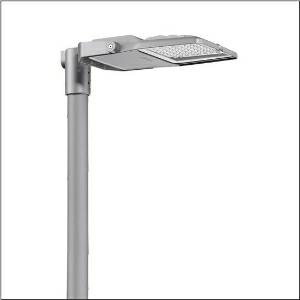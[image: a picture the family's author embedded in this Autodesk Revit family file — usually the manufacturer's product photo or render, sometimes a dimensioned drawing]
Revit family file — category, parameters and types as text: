
# Revit family: floodlight_fl_21_iq_mini___pl33t_5xa7772d4f3a_7ca2
name_source: partatom
category: Lighting Fixtures
units: mm (PartAtom-declared; Revit-internal decimal feet)

## family parameters
Cut with Voids When Loaded = No
Host = Face
Light Source = No
Part Type = Normal
Room Calculation Point = No
Round Connector Dimension = Use Diameter
Shared = No

## types (1)
- --- (1 x LED, 18390 lm, 143 W, 4000K)
    Apparent Load = 143 VA
    CIE Flux Codes = 26 75 99 100 100
    Color Rendering = 70
    Color Temperature = 4000K
    Default Elevation = 1800 mm
    Description = Floodlight FL 21 iQ mini, floodlight, primary light control with lens, of PMMA, primary optical cover: protective disc, of toughened safety glass, transparent, light distribution: PL33T, light emission: direct distribution, installation type: surface-mounted, LED, High Power LED, rated luminous flux: 18.390lm, luminous efficacy: 129lm/W, light colour: 740, colour temperature: 4000K, control gear: iQ Street-Remote/DALI, control: Auto-Match, Temp-Guard, Night-Set, Smart-Wire, Desk-Remote (wireless, voltage-free reading and setting of iQ features in the workshop via application-optimized NFC function/RFID function), optimised constant luminous flux control (CLO 2.0), Light-Fading, Lumen-Switch, with terminal, 6-pole, mains connection: 220..240V, AC, 50/60Hz, start of lifetime: 143W, end of service life: 152W, reduction: 61W, luminaire housing, of diecast aluminium, powder-coated, Siteco® metallic grey (DB 702S), corrosivity category C5 mid according to DIN EN ISO 12944, suitable for swimming pools, chlorine-resistant, sealing non-destructively replaceable, please order mast flange separately, mast bracket, of steel, galvanised, powder-coated, protection rating (complete): IP66, insulation class (complete): insulation class II (safety insulation), certification: CE, ENEC, VDE, protection symbol: D, impact resistance: IK08, permissible operating ambient temperature: -40..+40°C, permissible operating ambient temperature for outdoor applications: -40..+50°C, standard: DIN EN 12944, LABS conformity tested according to VDMA 24364:2018-05, packaging unit: 1 piece

Light Distribution: PL33T
    Height = 70 mm
    Lamp = 1 x LED
    Lamp Light Flux = 18390 lm
    Lamp Power = 143 W
    Lamp count = 1
    Length = 485 mm
    Luminous efficacy = 129 lm/W
    Manufacturer = Siteco
    ModVariant = No
    Model = 5XA7772D4F3A
    Number of Poles = 1
    OnlyDefault = Yes
    Power Factor = 1
    Product Name = Floodlight FL 21 iQ mini | PL33T
    Product group = floodlight | pylon annexe
    ProductGroupID = 6200
    Protection Class = Protection class II
    Protection Degree = IP 66
    RLX_Detail_Level = 1
    RLX_Emergency_Light_Flux = 0 lm
    RLX_Emergency_Type = 0
    RLX_Emergency_Type_DB = No
    RlxData = <blob elided: 101593 chars, md5=c9f020b6>
    Socket = socket
    Standby Power = 0 W
    System Light Flux = 18390 lm
    System Power = 143 W
    Type Comments = factory setting: luminous flux: 100 % | dim-lin: 254 | 730 mA
    Type Image = l_1007125.jpg
    URL = http://relux.com
    VarID = @adj_148780
    Voltage = 0 V
    Weight = 0.00 kg
    Width = 337 mm

## geometry (parser evidence)
native form markers: Blend x4, Sweep x11
no freeform markers — native parametric forms only
